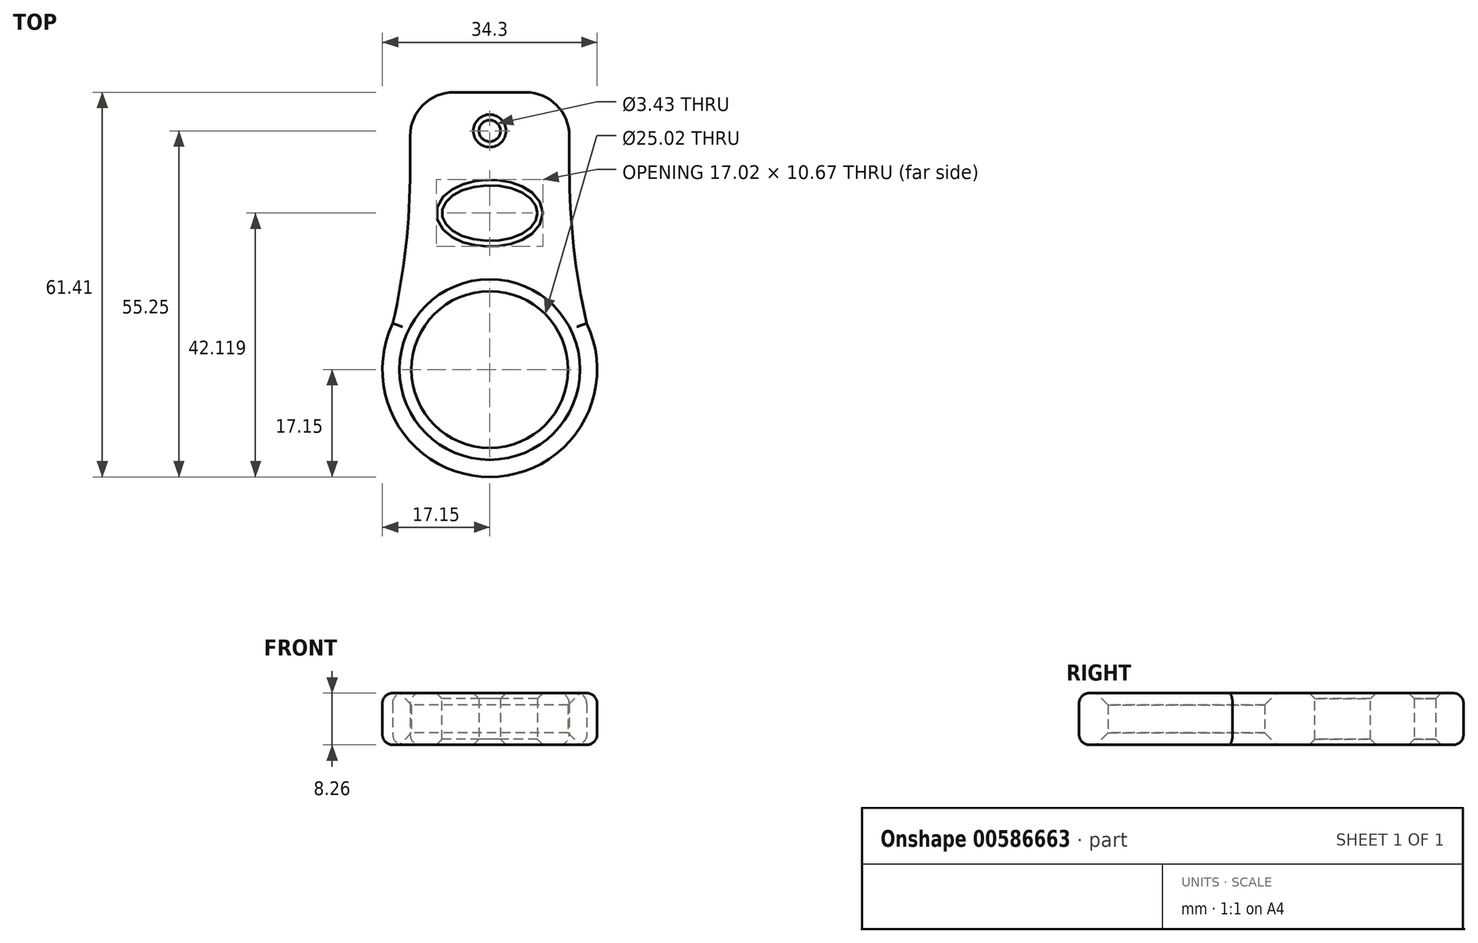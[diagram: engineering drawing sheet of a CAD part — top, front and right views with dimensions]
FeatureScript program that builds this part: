
annotation { "Feature Type Name" : "Feature", "Feature Type Description" : "" }
export const myFeature = defineFeature(function(context is Context, id is Id, definition is map)
    precondition{}
    {
        {
            var Q0;
            Q0=qCreatedBy(makeId("Top.planeOp"),FACE);
            var sketch = newSketch(context, id + "F0", { "sketchPlane" : qUnion([Q0])});
            skCircle(sketch, "E0", {"center": v(0, 0) * mm, "radius": 12.5 * mm});
            skCircle(sketch, "E1", {"center": v(0, 0) * mm, "radius": 17.15 * mm});
            skLineSegment(sketch, "E2.bottom", {"start": v(12.71, 44.26) * mm, "end": v(-12.71, 44.26) * mm});
            skLineSegment(sketch, "E2.top", {"start": v(12.71, 31.94) * mm, "end": v(-12.71, 31.94) * mm});
            skLineSegment(sketch, "E2.left", {"start": v(12.71, 44.26) * mm, "end": v(12.71, 31.94) * mm});
            skLineSegment(sketch, "E2.right", {"start": v(-12.71, 44.26) * mm, "end": v(-12.71, 31.94) * mm});
            skPoint(sketch, "E2.middle", {"position": v(0, 38.1) * mm});
            skArc(sketch, "E3", {"start": v(-12.71, 31.94) * mm, "mid": v(-13.82, 16.35) * mm, "end": v(-17.11, 1.08) * mm});
            skArc(sketch, "E4", {"start": v(12.71, 31.94) * mm, "mid": v(13.82, 16.36) * mm, "end": v(17.11, 1.09) * mm});
            skCircle(sketch, "E5", {"center": v(0, 38.1) * mm, "radius": 1.71 * mm});
            skEllipse(sketch, "E6", {"center": v(0, 24.97) * mm, "majorRadius": 7.62 * mm, "minorRadius": 4.45 * mm, "majorAxis": v(1, 0)});
            skSolve(sketch);
        }
        {
            var Q0;
            Q0 = qSketchRegion(id + "F0", true);
            extrude(context, id + "F1", {"entities" : qUnion([Q0]), "depth" : 8.25 * mm, "offsetDistance" : 25.4 * mm});
        }
        {
            var Q0;
            Q0=makeQuery(id+"F1.opExtrude","SWEPT_EDGE",EDGE,{"disambiguationData":[OSD([sQuery(id+"F0.wireOp",EDGE,"E2.bottom"),sQuery(id+"F0.wireOp",EDGE,"E2.right")])]});
            var Q1;
            Q1=makeQuery(id+"F1.opExtrude","SWEPT_EDGE",EDGE,{"disambiguationData":[OSD([sQuery(id+"F0.wireOp",EDGE,"E2.bottom"),sQuery(id+"F0.wireOp",EDGE,"E2.left")])]});
            fillet(context, id + "F2", {"entities" : qUnion([Q0, Q1]), "radius" : 7 * mm, "tangentPropagation" : true, "allowEdgeOverflow" : false});
        }
        {
            var Q0;
            Q0=makeQuery(id+"F1.opExtrude","CAP_EDGE",EDGE,{"disambiguationData":[OSD([sQuery(id+"F0.wireOp",EDGE,"E5")])],"isStart":false});
            var Q1;
            Q1=makeQuery(id+"F1.opExtrude","CAP_EDGE",EDGE,{"disambiguationData":[OSD([sQuery(id+"F0.wireOp",EDGE,"E5")])],"isStart":true});
            var Q2;
            Q2=makeQuery(id+"F1.opExtrude","CAP_EDGE",EDGE,{"disambiguationData":[OSD([sQuery(id+"F0.wireOp",EDGE,"E6")])],"isStart":false});
            var Q3;
            Q3=makeQuery(id+"F1.opExtrude","CAP_EDGE",EDGE,{"disambiguationData":[OSD([sQuery(id+"F0.wireOp",EDGE,"E6")])],"isStart":true});
            chamfer(context, id + "F3", {"entities" : qUnion([Q0, Q1, Q2, Q3]), "width" : 0.89 * mm, "tangentPropagation" : true});
        }
        {
            var Q0;
            Q0=makeQuery(id+"F1.opExtrude","CAP_EDGE",EDGE,{"disambiguationData":[OSD([sQuery(id+"F0.wireOp",EDGE,"E3")])],"isStart":true});
            var Q1;
            Q1=makeQuery(id+"F1.opExtrude","CAP_EDGE",EDGE,{"disambiguationData":[OSD([sQuery(id+"F0.wireOp",EDGE,"E1")])],"isStart":true});
            var Q2;
            Q2=makeQuery(id+"F1.opExtrude","CAP_EDGE",EDGE,{"disambiguationData":[OSD([sQuery(id+"F0.wireOp",EDGE,"E3")])],"isStart":false});
            var Q3;
            Q3=makeQuery(id+"F1.opExtrude","CAP_EDGE",EDGE,{"disambiguationData":[OSD([sQuery(id+"F0.wireOp",EDGE,"E1")])],"isStart":false});
            fillet(context, id + "F4", {"entities" : qUnion([Q0, Q1, Q2, Q3]), "radius" : 1.65 * mm, "tangentPropagation" : true, "allowEdgeOverflow" : false});
        }
        {
            var Q0;
            Q0=makeQuery(id+"F1.opExtrude","CAP_EDGE",EDGE,{"disambiguationData":[OSD([sQuery(id+"F0.wireOp",EDGE,"E0")])],"isStart":false});
            var Q1;
            Q1=makeQuery(id+"F1.opExtrude","CAP_EDGE",EDGE,{"disambiguationData":[OSD([sQuery(id+"F0.wireOp",EDGE,"E0")])],"isStart":true});
            chamfer(context, id + "F5", {"entities" : qUnion([Q0, Q1]), "width" : 1.9 * mm, "tangentPropagation" : true});
        }
    });
